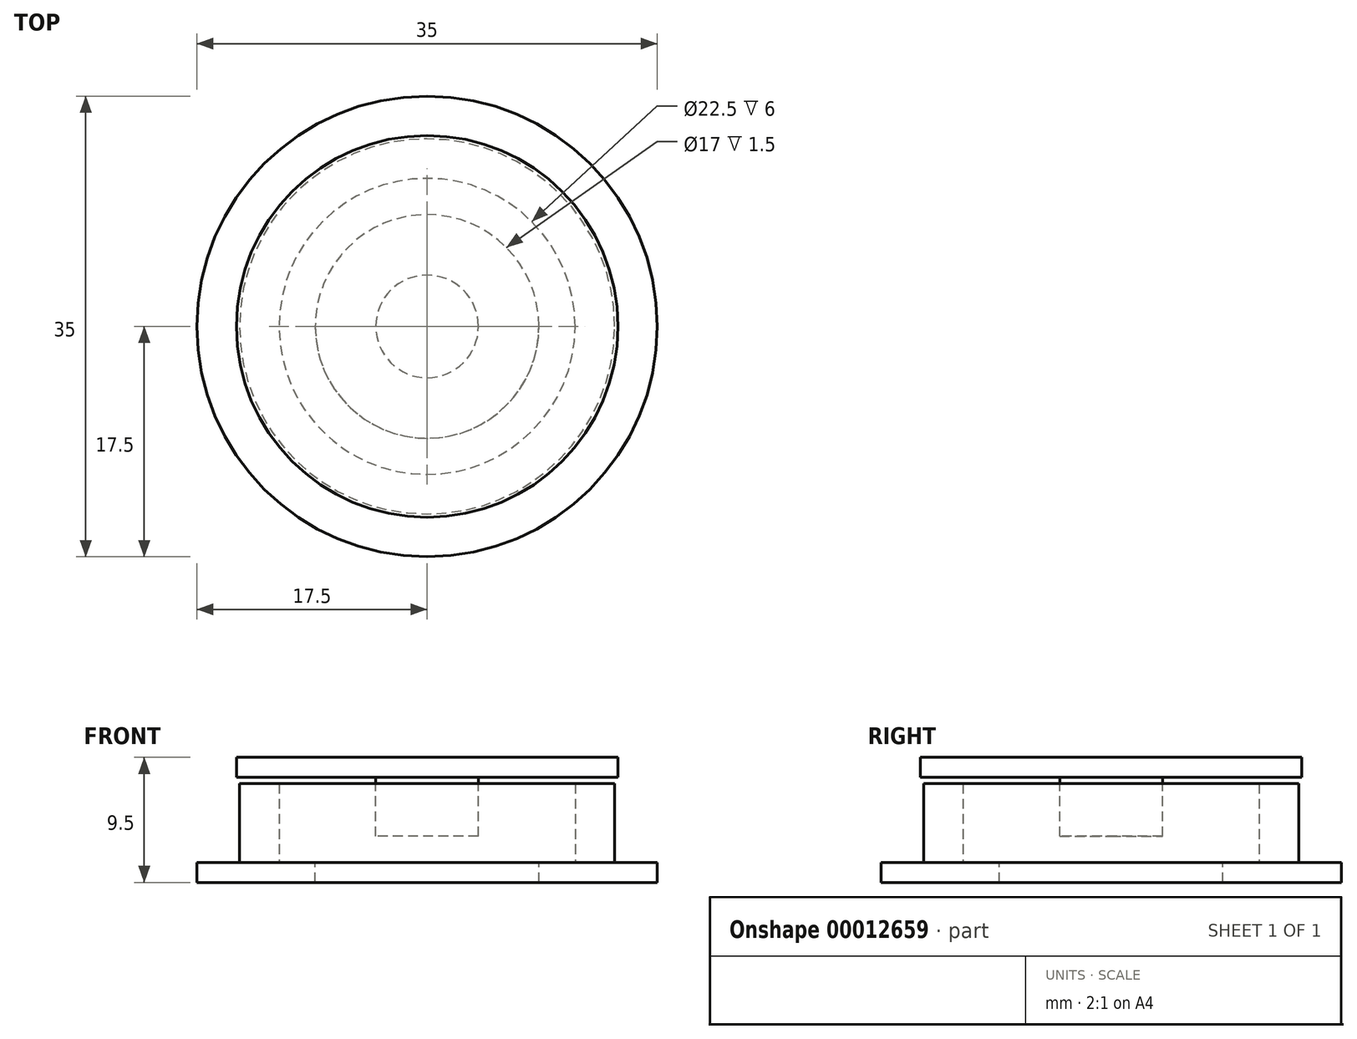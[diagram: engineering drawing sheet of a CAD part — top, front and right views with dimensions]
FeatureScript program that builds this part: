
annotation { "Feature Type Name" : "Feature", "Feature Type Description" : "" }
export const myFeature = defineFeature(function(context is Context, id is Id, definition is map)
    precondition{}
    {
        {
            var Q0;
            Q0=qCreatedBy(makeId("Top.planeOp"),FACE);
            var sketch = newSketch(context, id + "F0", { "sketchPlane" : qUnion([Q0])});
            skCircle(sketch, "E0", {"center": v(0, 0) * mm, "radius": 11.25 * mm});
            skCircle(sketch, "E1.0", {"center": v(0, 0) * mm, "radius": 14.25 * mm});
            skSolve(sketch);
        }
        {
            var Q0;
            Q0 = qSketchRegion(id + "F0", true);
            extrude(context, id + "F1", {"entities" : qUnion([Q0]), "depth" : 6 * mm});
        }
        {
            var Q0;
            Q0=makeQuery(id+"F1.opExtrude","CAP_FACE",FACE,{"disambiguationData":[OSD([sQuery(id+"F0.wireOp",EDGE,"E0"),sQuery(id+"F0.wireOp",EDGE,"E1.0")])],"isStart":true});
            var sketch = newSketch(context, id + "F2", { "sketchPlane" : qUnion([Q0])});
            skCircle(sketch, "E2", {"center": v(0, 0) * mm, "radius": 17.5 * mm});
            skSolve(sketch);
        }
        {
            var Q0;
            Q0 = qSketchRegion(id + "F2", true);
            extrude(context, id + "F3", {"entities" : qUnion([Q0]), "operationType" : NewBodyOperationType.ADD, "depth" : 1.5 * mm});
        }
        {
            var Q0;
            Q0=makeQuery(id+"F1.opExtrude","CAP_FACE",FACE,{"disambiguationData":[OSD([sQuery(id+"F0.wireOp",EDGE,"E0"),sQuery(id+"F0.wireOp",EDGE,"E1.0")])],"isStart":false});
            var sketch = newSketch(context, id + "F4", { "sketchPlane" : qUnion([Q0])});
            skCircle(sketch, "E3", {"center": v(0, 0) * mm, "radius": 3.9 * mm});
            skSolve(sketch);
        }
        {
            var Q0;
            Q0 = qSketchRegion(id + "F4", true);
            extrude(context, id + "F5", {"entities" : qUnion([Q0]), "oppositeDirection" : true, "depth" : 4 * mm, "hasSecondDirection" : true, "secondDirectionOppositeDirection" : false, "secondDirectionDepth" : .5 * mm});
        }
        {
            var Q0;
            Q0=makeQuery(id+"F5.opExtrude","CAP_FACE",FACE,{"disambiguationData":[OSD([sQuery(id+"F4.wireOp",EDGE,"E3")])],"isStart":true});
            var sketch = newSketch(context, id + "F6", { "sketchPlane" : qUnion([Q0])});
            skCircle(sketch, "E4", {"center": v(0, 0) * mm, "radius": 14.5 * mm});
            skSolve(sketch);
        }
        {
            var Q0;
            Q0=makeQuery(id+"F6.imprint","IMPRINT",FACE,{"disambiguationData":[TD([[makeQuery(id+"F6.imprint","IMPRINT",EDGE,{"derivedFrom":makeQuery(id+"F5.opExtrude","CAP_EDGE",EDGE,{"disambiguationData":[OSD([sQuery(id+"F4.wireOp",EDGE,"E3")])],"isStart":true})}),1.0]])]});
            var Q1;
            Q1=makeQuery(id+"F6.imprint","IMPRINT",FACE,{"disambiguationData":[TD([[makeQuery(id+"F6.imprint","IMPRINT",EDGE,{"derivedFrom":sQuery(id+"F6.wireOp",EDGE,"E4")}),1.0]])]});
            extrude(context, id + "F7", {"entities" : qUnion([Q0, Q1]), "operationType" : NewBodyOperationType.ADD, "depth" : 1.5 * mm});
        }
        {
            var Q0;
            Q0=makeQuery(id+"F3.boolean.opBoolean","SPLIT",FACE,{"disambiguationData":[TD([makeQuery(id+"F1.opExtrude","SWEPT_FACE",FACE,{"disambiguationData":[OSD([sQuery(id+"F0.wireOp",EDGE,"E0")])]})])],"derivedFrom":makeQuery(id+"F3.opExtrude","CAP_FACE",FACE,{"disambiguationData":[OSD([sQuery(id+"F2.wireOp",EDGE,"E2")])],"isStart":true})});
            var sketch = newSketch(context, id + "F8", { "sketchPlane" : qUnion([Q0])});
            skCircle(sketch, "E5", {"center": v(0, 0) * mm, "radius": 8.5 * mm});
            skSolve(sketch);
        }
        {
            var Q0;
            Q0=makeQuery(id+"F8.imprint","IMPRINT",FACE,{"disambiguationData":[TD([[makeQuery(id+"F8.imprint","IMPRINT",EDGE,{"derivedFrom":sQuery(id+"F8.wireOp",EDGE,"E5")}),1.0]])]});
            extrude(context, id + "F9", {"entities" : qUnion([Q0]), "operationType" : NewBodyOperationType.REMOVE, "oppositeDirection" : true, "depth" : 5 * mm});
        }
    });
